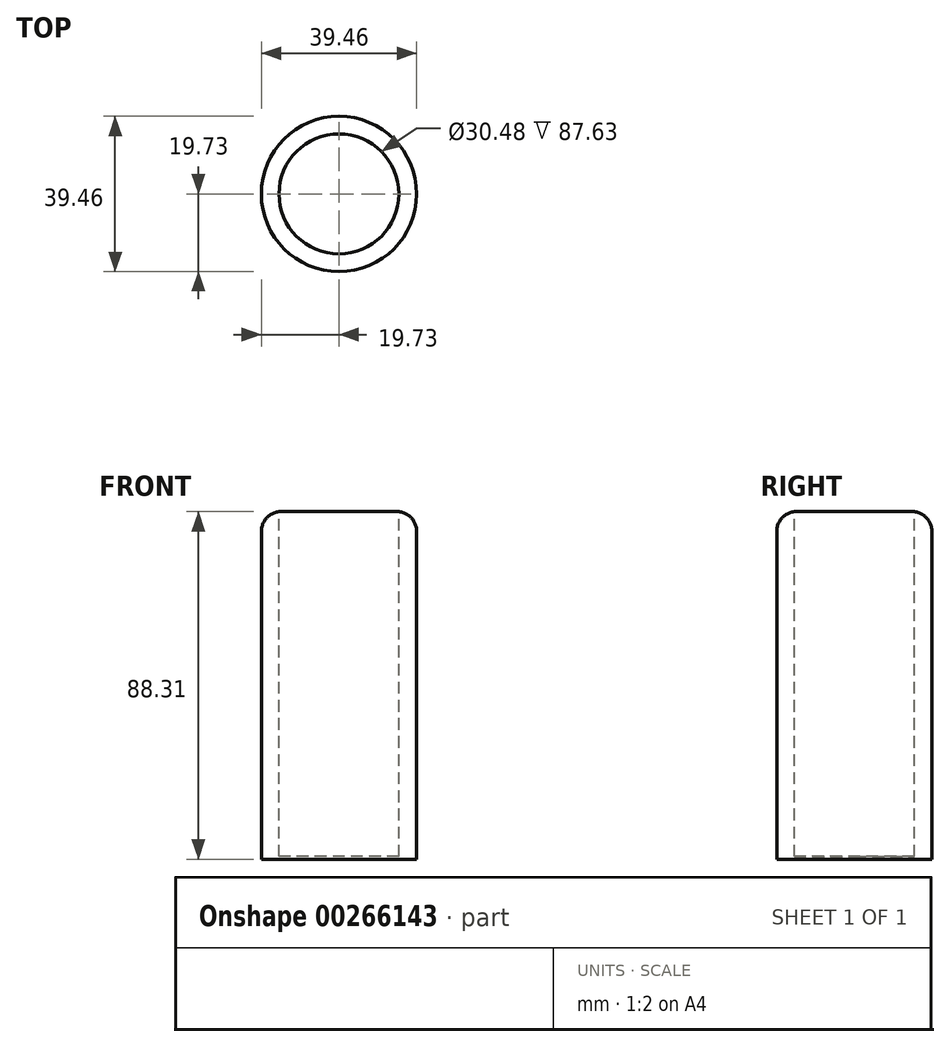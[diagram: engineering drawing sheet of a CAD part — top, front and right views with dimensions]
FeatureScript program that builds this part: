
annotation { "Feature Type Name" : "Feature", "Feature Type Description" : "" }
export const myFeature = defineFeature(function(context is Context, id is Id, definition is map)
    precondition{}
    {
        {
            var Q0;
            Q0=qCreatedBy(makeId("Front.planeOp"),FACE);
            var sketch = newSketch(context, id + "F0", { "sketchPlane" : qUnion([Q0])});
            skLineSegment(sketch, "E0", {"start": v(0, 75.95) * mm, "end": v(0, -75.95) * mm});
            skLineSegment(sketch, "E1", {"start": v(0, 28.4) * mm, "end": v(19.73, 28.4) * mm});
            skLineSegment(sketch, "E2", {"start": v(19.73, 28.4) * mm, "end": v(19.73, -59.92) * mm});
            skLineSegment(sketch, "E3", {"start": v(19.73, -59.92) * mm, "end": v(0, -59.92) * mm});
            skSolve(sketch);
        }
        {
            var Q0;
            {var subQ0=sQuery(id+"F0.wireOp",EDGE,"E1");Q0=makeQuery(id+"F0.imprint","IMPRINT",FACE,{"disambiguationData":[TD([[makeQuery(id+"F0.imprint","IMPRINT",EDGE,{"derivedFrom":subQ0}),-1.0]])]});}
            var Q1;
            Q1=sQuery(id+"F0.wireOp",EDGE,"E0");
            revolve(context, id + "F1", {"entities" : qUnion([Q0]), "axis" : qUnion([Q1]), "revolveType" : RevolveType.FULL});
        }
        {
            var Q0;
            Q0=makeQuery(id+"F1.opRevolve","SWEPT_FACE",FACE,{"disambiguationData":[OSD([sQuery(id+"F0.wireOp",EDGE,"E1")])]});
            var sketch = newSketch(context, id + "F2", { "sketchPlane" : qUnion([Q0])});
            skCircle(sketch, "E4", {"center": v(0, 0) * mm, "radius": 15.24 * mm});
            skSolve(sketch);
        }
        {
            var Q0;
            Q0 = qSketchRegion(id + "F2", true);
            extrude(context, id + "F3", {"entities" : qUnion([Q0]), "operationType" : NewBodyOperationType.REMOVE, "oppositeDirection" : true, "depth" : 87.63 * mm});
        }
        {
            var Q0;
            Q0=makeQuery(id+"F1.opRevolve","SWEPT_EDGE",EDGE,{"disambiguationData":[OSD([sQuery(id+"F0.wireOp",EDGE,"E1"),sQuery(id+"F0.wireOp",EDGE,"E2")])]});
            fillet(context, id + "F4", {"entities" : qUnion([Q0]), "radius" : 5.08 * mm, "tangentPropagation" : true, "allowEdgeOverflow" : false});
        }
    });
